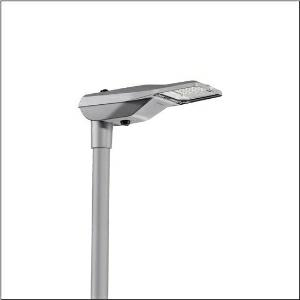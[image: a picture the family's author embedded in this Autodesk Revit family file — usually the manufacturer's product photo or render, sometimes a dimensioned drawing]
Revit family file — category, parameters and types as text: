
# Revit family: streetlight_sl_21_iq_micro___st1_0a_5xe1d61y08cb_da7e
name_source: partatom
category: Lighting Fixtures
units: mm (PartAtom-declared; Revit-internal decimal feet)

## family parameters
Cut with Voids When Loaded = No
Host = Face
Light Source = No
Part Type = Normal
Room Calculation Point = No
Round Connector Dimension = Use Diameter
Shared = No

## types (1)
- --- (1 x LED, 2500 lm, 19.1 W, 2700K)
    Apparent Load = 19 VA
    CIE Flux Codes = 37 72 97 100 100
    Color Rendering = 70
    Color Temperature = 2700K
    Default Elevation = 1800 mm
    Description = Streetlight SL 21 iQ micro, mast luminaire, primary light control with lens, of PMMA, primary optical cover: cover, of toughened safety glass, transparent, light distribution: ST1.0a, light emission: direct distribution, primary light characteristic: asymmetric, installation type: post-top, side-entry, LED, High Power LED, rated luminous flux: 2.500lm, luminous efficacy: 131lm/W, light colour: 727, colour temperature: 2700K, control gear: iQ-Street Remote, D4i with power reduction, control: pre-setting: logarithmic dimming characteristic, Street-Remote, Auto-Match, Temp-Guard, Lumen-Switch, Night-Set, Smart-Wire, Light-Fading, Desk-Remote (wireless, voltage-free reading and setting of iQ features in the workshop via application-optimized NFC function/RFID function), optimised constant luminous flux control (CLO 2.0), mains connection: 220..240V, AC, 50/60Hz, start of lifetime: 19W, end of service life: 20W, reduction: 9W, luminaire housing, of diecast aluminium, powder-coated, Siteco® metallic grey (DB 702S), corrosivity category C5 mid according to DIN EN ISO 12944, please order mast flange separately, inclination adjustable: 0°, 5°, 10°, 15°, sealing non-destructively replaceable, multi-level sealing system, length: 528mm, width: 235mm, height: 110mm, mast flange for spigot size: 42mm (side-entry): 5XC10008XM4, 60/48mm (side-entry/post-top): 5XC10108XM2, 76/60mm (side-entry/post-top): 5XC10108XM1, mounting height: 4..8m, Smart Interface below and above, protection rating (complete): IP66, insulation class (complete): insulation class II (safety insulation), certification: CE, ENEC, ENEC+, VDE, impact resistance: IK10, permissible operating ambient temperature for outdoor applications: -40..+50°C, standard-compliant lighting for roads and squares, packaging unit: 1 piece

Light Distribution: ST1.0a
    Height = 110 mm
    Lamp = 1 x LED
    Lamp Light Flux = 2500 lm
    Lamp Power = 19.1 W
    Lamp count = 1
    Length = 528 mm
    Luminous efficacy = 131 lm/W
    Manufacturer = Siteco
    ModVariant = No
    Model = 5XE1D61Y08CB
    Number of Poles = 1
    OnlyDefault = Yes
    Power Factor = 1
    Product Name = Streetlight SL 21 iQ micro | ST1.0a
    Product group = mast luminaire | pylon top
    ProductGroupID = 6100
    Protection Class = Protection class II
    Protection Degree = IP 66
    RLX_Detail_Level = 1
    RLX_Emergency_Light_Flux = 0 lm
    RLX_Emergency_Type = 0
    RLX_Emergency_Type_DB = No
    RlxData = <blob elided: 98333 chars, md5=60b693f4>
    Socket = socket
    Standby Power = 0 W
    System Light Flux = 2500 lm
    System Power = 19 W
    Type Comments = factory setting: luminous flux: 100 % | dim-lin: 254 | 387 mA
    Type Image = l_1007239.jpg
    URL = http://relux.com
    VarID = @adj_115532
    Voltage = 0 V
    Weight = 0.00 kg
    Width = 235 mm

## geometry (parser evidence)
native form markers: Blend x4, Sweep x11
no freeform markers — native parametric forms only
